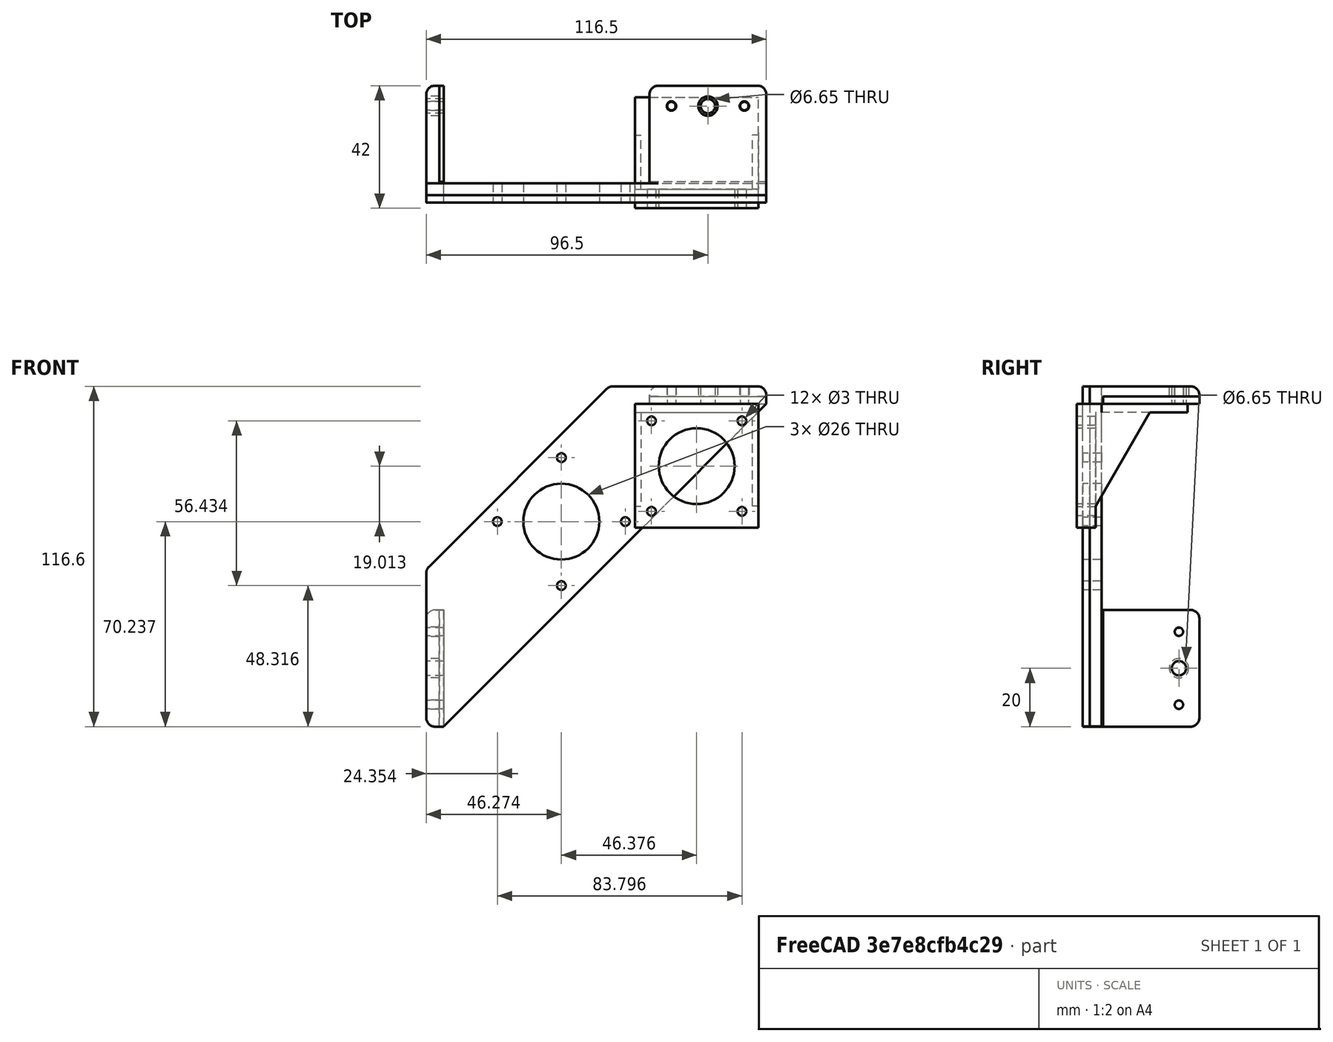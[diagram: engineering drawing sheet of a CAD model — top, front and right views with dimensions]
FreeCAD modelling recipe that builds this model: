
FCSTD DOCUMENT  (FreeCAD 0.18.4R)
Label: Stepper_Motor_Mount
License: All rights reserved
LicenseURL: http://en.wikipedia.org/wiki/All_rights_reserved
objects: Part::Cut×36, Part::Box×21, Part::Cylinder×15, Part::FeaturePython×12, Part::MultiFuse×11, Part::Fillet×6, Part::Prism×2
note: 103 computed .brp shape members not serialized (recipe doc carries the construction recipe); baked Part::Feature solids carry a one-line shape summary decoded from their .brp

FEATURE [Part::Box] Box007  label="Cube007"
  AttacherType = Attacher::AttachEngine3D
  Height = 42.3
  Length = 42.3
  Placement = pos=(0,-21,0) rot=(0,0,1;0rad)
  Width = 6.5
FEATURE [Part::Cylinder] Cylinder001
  Angle = 360
  AttacherType = Attacher::AttachEngine3D
  Height = 10
  Placement = pos=(5.65,-14,5.65) rot=(1,0,0;1.5708rad)
  Radius = 1.5
FEATURE [Part::Cylinder] Cylinder002
  Angle = 360
  AttacherType = Attacher::AttachEngine3D
  Height = 10
  Placement = pos=(5.65,-14,36.65) rot=(1,0,0;1.5708rad)
  Radius = 1.5
FEATURE [Part::Cylinder] Cylinder003
  Angle = 360
  AttacherType = Attacher::AttachEngine3D
  Height = 10
  Placement = pos=(36.65,-14,5.65) rot=(1,0,0;1.5708rad)
  Radius = 1.5
FEATURE [Part::Cylinder] Cylinder004
  Angle = 360
  AttacherType = Attacher::AttachEngine3D
  Height = 10
  Placement = pos=(36.65,-14,36.65) rot=(1,0,0;1.5708rad)
  Radius = 1.5
FEATURE [Part::Cut] Cut007
  Base = -> Box007
  Tool = -> Cylinder001
FEATURE [Part::Cut] Cut008
  Base = -> Cut007
  Tool = -> Cylinder004
FEATURE [Part::Cut] Cut009
  Base = -> Cut008
  Tool = -> Cylinder003
FEATURE [Part::Cut] Cut010
  Base = -> Cut009
  Tool = -> Cylinder002
FEATURE [Part::Cylinder] Cylinder005
  Angle = 360
  AttacherType = Attacher::AttachEngine3D
  Height = 10
  Placement = pos=(21.15,-14,21.15) rot=(1,0,0;1.5708rad)
  Radius = 13
FEATURE [Part::Cut] Cut011
  Base = -> Cut010
  Placement = pos=(0,-7,-31.5) rot=(0,0,1;0rad)
  Tool = -> Cylinder005
FEATURE [Part::Box] Box008  label="Cube008"
  AttacherType = Attacher::AttachEngine3D
  Height = 3
  Length = 42.3
  Placement = pos=(0,-28,8) rot=(0,0,1;0rad)
  Width = 38
FEATURE [Part::MultiFuse] Fusion001
  Shapes = -> [Cut011,Box008]
FEATURE [Part::Prism] Prism001
  AttacherType = Attacher::AttachEngine3D
  Circumradius = 23
  Height = 2
  Placement = pos=(0,-19,2) rot=(0,1,0;1.5708rad)
  Polygon = 3
FEATURE [Part::Box] Box009  label="Cube009"
  AttacherType = Attacher::AttachEngine3D
  Height = 70
  Length = 44
  Placement = pos=(0,-43,-25.5) rot=(0,0,1;0rad)
  Width = 24
FEATURE [Part::Cut] Cut012
  Base = -> Prism001
  Placement = pos=(0,-3,-4) rot=(0,0,1;0rad)
  Tool = -> Box009
FEATURE [Part::Box] Box010  label="Cube010"
  AttacherType = Attacher::AttachEngine3D
  Height = 70
  Length = 44
  Placement = pos=(0,-43,-25.5) rot=(0,0,1;0rad)
  Width = 24
FEATURE [Part::Prism] Prism002
  AttacherType = Attacher::AttachEngine3D
  Circumradius = 23
  Height = 2
  Placement = pos=(0,-19,2) rot=(0,1,0;1.5708rad)
  Polygon = 3
FEATURE [Part::Cut] Cut013
  Base = -> Prism002
  Placement = pos=(40.3,-3,-4) rot=(0,0,1;0rad)
  Tool = -> Box010
FEATURE [Part::MultiFuse] Fusion002
  Shapes = -> [Fusion001,Cut012]
FEATURE [Part::MultiFuse] Fusion003  label="MotorMountV1"
  Shapes = -> [Cut013,Fusion002]
FEATURE [Part::Box] Box019  label="Cube019"
  AttacherType = Attacher::AttachEngine3D
  Height = 42.3
  Length = 42.3
  Placement = pos=(0,-21,0) rot=(0,0,1;0rad)
  Width = 6.5
FEATURE [Part::Cylinder] Cylinder007
  Angle = 360
  AttacherType = Attacher::AttachEngine3D
  Height = 10
  Placement = pos=(5.65,-14,5.65) rot=(1,0,0;1.5708rad)
  Radius = 1.5
FEATURE [Part::Cylinder] Cylinder008
  Angle = 360
  AttacherType = Attacher::AttachEngine3D
  Height = 10
  Placement = pos=(5.65,-14,36.65) rot=(1,0,0;1.5708rad)
  Radius = 1.5
FEATURE [Part::Cylinder] Cylinder009
  Angle = 360
  AttacherType = Attacher::AttachEngine3D
  Height = 10
  Placement = pos=(36.65,-14,5.65) rot=(1,0,0;1.5708rad)
  Radius = 1.5
FEATURE [Part::Cylinder] Cylinder010
  Angle = 360
  AttacherType = Attacher::AttachEngine3D
  Height = 10
  Placement = pos=(36.65,-14,36.65) rot=(1,0,0;1.5708rad)
  Radius = 1.5
FEATURE [Part::Cut] Cut027
  Base = -> Box019
  Tool = -> Cylinder007
FEATURE [Part::Cut] Cut028
  Base = -> Cut027
  Tool = -> Cylinder010
FEATURE [Part::Cut] Cut029
  Base = -> Cut028
  Tool = -> Cylinder009
FEATURE [Part::Cut] Cut030
  Base = -> Cut029
  Tool = -> Cylinder008
FEATURE [Part::Cylinder] Cylinder011
  Angle = 360
  AttacherType = Attacher::AttachEngine3D
  Height = 10
  Placement = pos=(21.15,-14,21.15) rot=(1,0,0;1.5708rad)
  Radius = 13
FEATURE [Part::Cut] Cut031
  Base = -> Cut030
  Placement = pos=(0,-7,-31.5) rot=(0,0,1;0rad)
  Tool = -> Cylinder011
FEATURE [Part::Box] Box020  label="Cube020"
  AttacherType = Attacher::AttachEngine3D
  Height = 42.3
  Length = 57
  Placement = pos=(42.3,-28,-31.5) rot=(0,0,1;0rad)
  Width = 6.5
FEATURE [Part::Box] Box021  label="Cube021"
  AttacherType = Attacher::AttachEngine3D
  Height = 42.3
  Length = 57
  Placement = pos=(-57,-28,-31.5) rot=(0,0,1;0rad)
  Width = 6.5
FEATURE [Part::MultiFuse] Fusion004
  Shapes = -> [Cut031,Box020]
FEATURE [Part::MultiFuse] Fusion005
  Placement = pos=(-47.5,2,-37) rot=(0,-1,0;0.785398rad)
  Shapes = -> [Fusion004,Box021]
FEATURE [Part::Box] Box022  label="Cube022"
  AttacherType = Attacher::AttachEngine3D
  Height = 6
  Length = 40
  Placement = pos=(5,-26,11) rot=(0,0,1;0rad)
  Width = 40
FEATURE [Part::Box] Box023  label="Cube023"
  AttacherType = Attacher::AttachEngine3D
  Height = 34
  Length = 81
  Placement = pos=(-21,-26,17) rot=(0,0,1;0rad)
  Width = 40
FEATURE [Part::Cut] Cut032
  Base = -> Fusion005
  Tool = -> Box023
FEATURE [Part::FeaturePython] ScrewTap005  label="M6x20.0-ScrewTap"  # Fasteners workbench fastener (typed FeaturePython)
  Placement = pos=(25,7,21) rot=(0,0,1;0rad)
  diameter = 8
  invert = false
  length = 20
  matchOuter = false
  offset = 0
  thread = false
FEATURE [Part::Cut] Cut033
  Base = -> Box022
  Tool = -> ScrewTap005
FEATURE [Part::FeaturePython] ScrewTap006  label="(M3.5)x20.0-ScrewTap004"  # Fasteners workbench fastener (typed FeaturePython)
  Placement = pos=(12.5,7,22) rot=(0,0,1;0rad)
  diameter = 5
  invert = false
  length = 20
  matchOuter = false
  offset = 0
  thread = false
FEATURE [Part::FeaturePython] ScrewTap007  label="(M3.5)x20.0-ScrewTap005"  # Fasteners workbench fastener (typed FeaturePython)
  Placement = pos=(37.5,7,22) rot=(0,0,1;0rad)
  diameter = 5
  invert = false
  length = 20
  matchOuter = false
  offset = 0
  thread = false
FEATURE [Part::Cut] Cut034
  Base = -> Cut033
  Tool = -> ScrewTap006
FEATURE [Part::Cut] Cut035
  Base = -> Cut034
  Tool = -> ScrewTap007
FEATURE [Part::Fillet] Fillet
  Base = -> Cut035
  Edges = 2 edges r=3: [Edge3,Edge14]
FEATURE [Part::Box] Box024  label="Cube024"
  AttacherType = Attacher::AttachEngine3D
  Height = 6
  Length = 40
  Placement = pos=(5,-26,11) rot=(0,0,1;0rad)
  Width = 40
FEATURE [Part::FeaturePython] ScrewTap008  label="M6x20.0-ScrewTap001"  # Fasteners workbench fastener (typed FeaturePython)
  Placement = pos=(25,7,21) rot=(0,0,1;0rad)
  diameter = 8
  invert = false
  length = 20
  matchOuter = false
  offset = 0
  thread = false
FEATURE [Part::Cut] Cut037
  Base = -> Box024
  Tool = -> ScrewTap008
FEATURE [Part::FeaturePython] ScrewTap009  label="(M3.5)x20.0-ScrewTap006"  # Fasteners workbench fastener (typed FeaturePython)
  Placement = pos=(12.5,7,22) rot=(0,0,1;0rad)
  diameter = 5
  invert = false
  length = 20
  matchOuter = false
  offset = 0
  thread = false
FEATURE [Part::Cut] Cut036
  Base = -> Cut037
  Tool = -> ScrewTap009
FEATURE [Part::FeaturePython] ScrewTap010  label="(M3.5)x20.0-ScrewTap007"  # Fasteners workbench fastener (typed FeaturePython)
  Placement = pos=(37.5,7,22) rot=(0,0,1;0rad)
  diameter = 5
  invert = false
  length = 20
  matchOuter = false
  offset = 0
  thread = false
FEATURE [Part::Cut] Cut038
  Base = -> Cut036
  Tool = -> ScrewTap010
FEATURE [Part::Fillet] Fillet001
  Base = -> Cut038
  Edges = 2 edges r=3: [Edge3,Edge14]
  Placement = pos=(-82.5,0,-54.6) rot=(0,1,0;1.5708rad)
FEATURE [Part::Box] Box025  label="Cube025"
  AttacherType = Attacher::AttachEngine3D
  Height = 34
  Length = 81
  Placement = pos=(-105.5,-26,-37.6) rot=(0,1,0;1.5708rad)
  Width = 40
FEATURE [Part::Cut] Cut039
  Base = -> Cut032
  Tool = -> Box025
FEATURE [Part::MultiFuse] Fusion006
  Shapes = -> [Cut039,Fillet001]
FEATURE [Part::MultiFuse] Fusion007
  Shapes = -> [Fusion006,Fillet]
FEATURE [Part::Fillet] Fillet002  label="MotorMountV2"
  Base = -> Fusion007
  Edges = 4 edges r=3: [Edge20,Edge47,Edge84,Edge111]
FEATURE [Part::Box] Box026  label="Cube026"
  AttacherType = Attacher::AttachEngine3D
  Height = 42.3
  Length = 42.3
  Placement = pos=(0,-21,0) rot=(0,0,1;0rad)
  Width = 6.5
FEATURE [Part::Cylinder] Cylinder012
  Angle = 360
  AttacherType = Attacher::AttachEngine3D
  Height = 10
  Placement = pos=(5.65,-14,5.65) rot=(1,0,0;1.5708rad)
  Radius = 1.5
FEATURE [Part::Cylinder] Cylinder013
  Angle = 360
  AttacherType = Attacher::AttachEngine3D
  Height = 10
  Placement = pos=(5.65,-14,36.65) rot=(1,0,0;1.5708rad)
  Radius = 1.5
FEATURE [Part::Cylinder] Cylinder014
  Angle = 360
  AttacherType = Attacher::AttachEngine3D
  Height = 10
  Placement = pos=(36.65,-14,5.65) rot=(1,0,0;1.5708rad)
  Radius = 1.5
FEATURE [Part::Cylinder] Cylinder015
  Angle = 360
  AttacherType = Attacher::AttachEngine3D
  Height = 10
  Placement = pos=(36.65,-14,36.65) rot=(1,0,0;1.5708rad)
  Radius = 1.5
FEATURE [Part::Cut] Cut040
  Base = -> Box026
  Tool = -> Cylinder012
FEATURE [Part::Cut] Cut041
  Base = -> Cut040
  Tool = -> Cylinder015
FEATURE [Part::Cut] Cut042
  Base = -> Cut041
  Tool = -> Cylinder014
FEATURE [Part::Cut] Cut043
  Base = -> Cut042
  Tool = -> Cylinder013
FEATURE [Part::Cylinder] Cylinder016
  Angle = 360
  AttacherType = Attacher::AttachEngine3D
  Height = 10
  Placement = pos=(21.15,-14,21.15) rot=(1,0,0;1.5708rad)
  Radius = 13
FEATURE [Part::Cut] Cut044
  Base = -> Cut043
  Placement = pos=(0,-7,-31.5) rot=(0,0,1;0rad)
  Tool = -> Cylinder016
FEATURE [Part::Box] Box027  label="Cube027"
  AttacherType = Attacher::AttachEngine3D
  Height = 42.3
  Length = 57
  Placement = pos=(42.3,-28,-31.5) rot=(0,0,1;0rad)
  Width = 6.5
FEATURE [Part::Box] Box028  label="Cube028"
  AttacherType = Attacher::AttachEngine3D
  Height = 42.3
  Length = 57
  Placement = pos=(-57,-28,-31.5) rot=(0,0,1;0rad)
  Width = 6.5
FEATURE [Part::MultiFuse] Fusion008
  Shapes = -> [Cut044,Box027]
FEATURE [Part::MultiFuse] Fusion009
  Placement = pos=(-47.5,2,-37) rot=(0,-1,0;0.785398rad)
  Shapes = -> [Fusion008,Box028]
FEATURE [Part::Box] Box029  label="Cube029"
  AttacherType = Attacher::AttachEngine3D
  Height = 6
  Length = 40
  Placement = pos=(5,-26,11) rot=(0,0,1;0rad)
  Width = 40
FEATURE [Part::Box] Box030  label="Cube030"
  AttacherType = Attacher::AttachEngine3D
  Height = 34
  Length = 81
  Placement = pos=(-21,-26,17) rot=(0,0,1;0rad)
  Width = 40
FEATURE [Part::Cut] Cut045
  Base = -> Fusion009
  Tool = -> Box030
FEATURE [Part::FeaturePython] ScrewTap011  label="M8x20.0-ScrewTap"  # Fasteners workbench fastener (typed FeaturePython)
  Placement = pos=(25,7,21) rot=(0,0,1;0rad)
  diameter = 9
  invert = false
  length = 20
  matchOuter = false
  offset = 0
  thread = false
FEATURE [Part::Cut] Cut046
  Base = -> Box029
  Tool = -> ScrewTap011
FEATURE [Part::FeaturePython] ScrewTap012  label="M4x20.0-ScrewTap001"  # Fasteners workbench fastener (typed FeaturePython)
  Placement = pos=(12.5,7,22) rot=(0,0,1;0rad)
  diameter = 6
  invert = false
  length = 20
  matchOuter = false
  offset = 0
  thread = false
FEATURE [Part::FeaturePython] ScrewTap013  label="M4x20.0-ScrewTap"  # Fasteners workbench fastener (typed FeaturePython)
  Placement = pos=(37.5,7,22) rot=(0,0,1;0rad)
  diameter = 6
  invert = false
  length = 20
  matchOuter = false
  offset = 0
  thread = false
FEATURE [Part::Cut] Cut047
  Base = -> Cut046
  Tool = -> ScrewTap012
FEATURE [Part::Cut] Cut048
  Base = -> Cut047
  Tool = -> ScrewTap013
FEATURE [Part::Fillet] Fillet003
  Base = -> Cut048
  Edges = 2 edges r=3: [Edge3,Edge14]
FEATURE [Part::Box] Box031  label="Cube031"
  AttacherType = Attacher::AttachEngine3D
  Height = 6
  Length = 40
  Placement = pos=(5,-26,11) rot=(0,0,1;0rad)
  Width = 40
FEATURE [Part::FeaturePython] ScrewTap014  label="M8x20.0-ScrewTap001"  # Fasteners workbench fastener (typed FeaturePython)
  Placement = pos=(25,7,21) rot=(0,0,1;0rad)
  diameter = 9
  invert = false
  length = 20
  matchOuter = false
  offset = 0
  thread = false
FEATURE [Part::Cut] Cut050
  Base = -> Box031
  Tool = -> ScrewTap014
FEATURE [Part::FeaturePython] ScrewTap015  label="M4x20.0-ScrewTap003"  # Fasteners workbench fastener (typed FeaturePython)
  Placement = pos=(12.5,7,22) rot=(0,0,1;0rad)
  diameter = 6
  invert = false
  length = 20
  matchOuter = false
  offset = 0
  thread = false
FEATURE [Part::Cut] Cut049
  Base = -> Cut050
  Tool = -> ScrewTap015
FEATURE [Part::FeaturePython] ScrewTap016  label="M4x20.0-ScrewTap002"  # Fasteners workbench fastener (typed FeaturePython)
  Placement = pos=(37.5,7,22) rot=(0,0,1;0rad)
  diameter = 6
  invert = false
  length = 20
  matchOuter = false
  offset = 0
  thread = false
FEATURE [Part::Cut] Cut051
  Base = -> Cut049
  Tool = -> ScrewTap016
FEATURE [Part::Fillet] Fillet004
  Base = -> Cut051
  Edges = 2 edges r=3: [Edge3,Edge14]
  Placement = pos=(-82.5,0,-54.6) rot=(0,1,0;1.5708rad)
FEATURE [Part::Box] Box032  label="Cube032"
  AttacherType = Attacher::AttachEngine3D
  Height = 34
  Length = 81
  Placement = pos=(-105.5,-26,-37.6) rot=(0,1,0;1.5708rad)
  Width = 40
FEATURE [Part::Cut] Cut052
  Base = -> Cut045
  Tool = -> Box032
FEATURE [Part::MultiFuse] Fusion010
  Shapes = -> [Cut052,Fillet004]
FEATURE [Part::MultiFuse] Fusion011
  Shapes = -> [Fusion010,Fillet003]
FEATURE [Part::Fillet] Fillet005  label="MotorMountV003"
  Base = -> Fusion011
  Edges = 4 edges r=3: [Edge20,Edge47,Edge84,Edge111]
FEATURE [Part::Box] Box033  label="Cube033"
  AttacherType = Attacher::AttachEngine3D
  Height = 10
  Length = 100
  Placement = pos=(-35,-19,3.5) rot=(0,0,1;0rad)
  Width = 100
FEATURE [Part::Box] Box034  label="Cube034"
  AttacherType = Attacher::AttachEngine3D
  Height = 100
  Length = 10
  Placement = pos=(-67,-19,-112.5) rot=(0,0,1;0rad)
  Width = 100
FEATURE [Part::Box] Box036  label="Cube036"
  AttacherType = Attacher::AttachEngine3D
  Height = 210
  Length = 210
  Placement = pos=(-77,-223.5,-108) rot=(0,0,1;0rad)
  Width = 200
FEATURE [Part::Cut] Cut053
  Base = -> Fillet005
  Tool = -> Box033
FEATURE [Part::Cut] Cut054
  Base = -> Cut053
  Tool = -> Box036
FEATURE [Part::Cut] Cut055  label="MotorMountV3"
  Base = -> Cut054
  Tool = -> Box034
